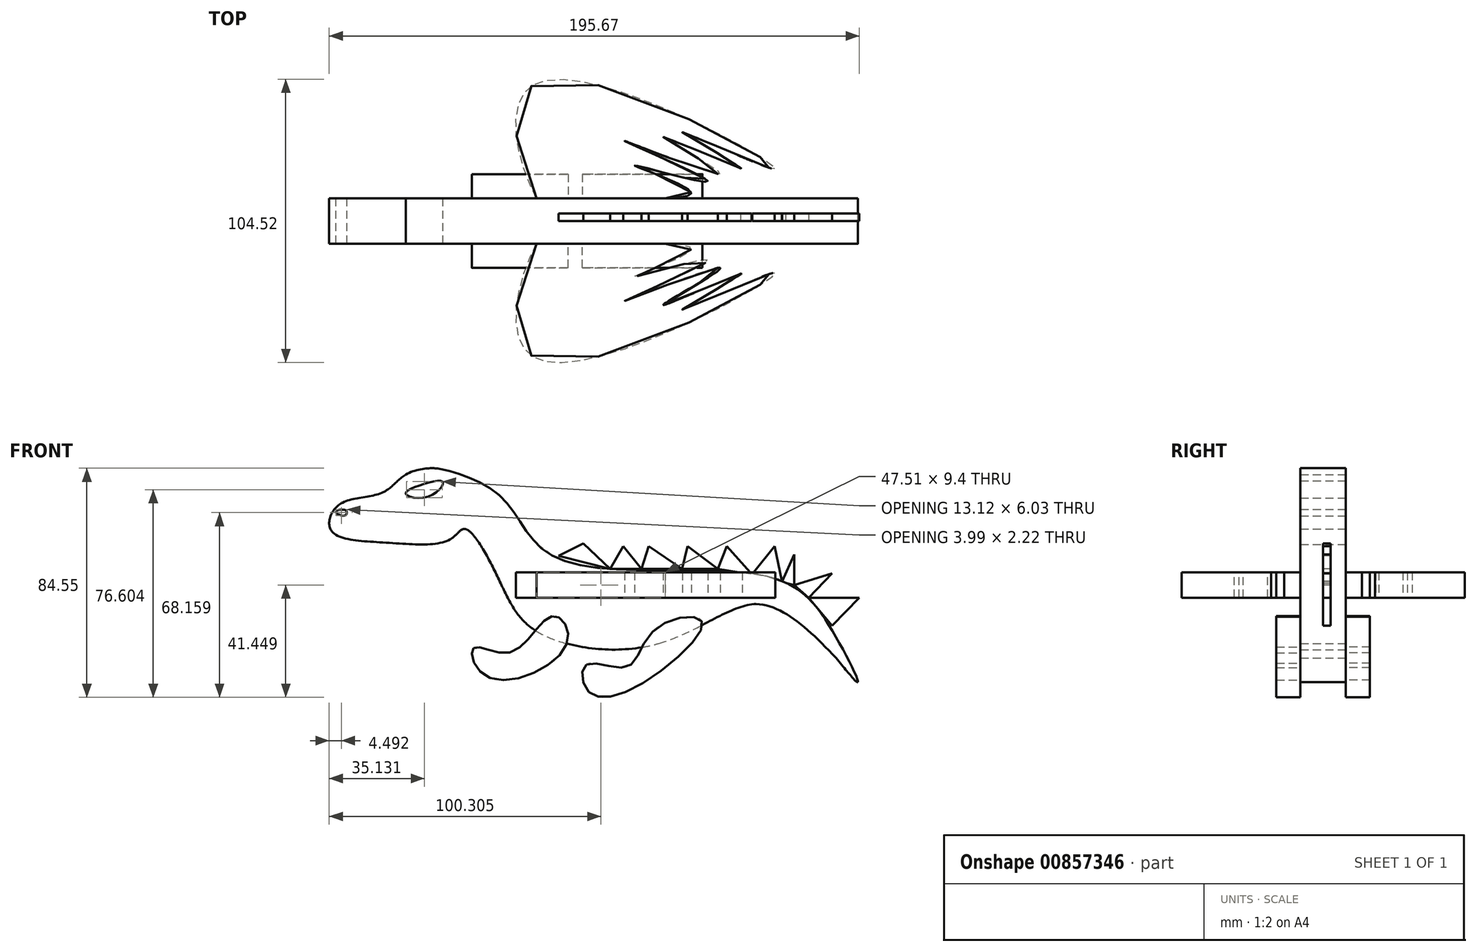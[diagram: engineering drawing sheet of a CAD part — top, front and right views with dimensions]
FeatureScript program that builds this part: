
annotation { "Feature Type Name" : "Feature", "Feature Type Description" : "" }
export const myFeature = defineFeature(function(context is Context, id is Id, definition is map)
    precondition{}
    {
        {
            var Q0;
            Q0=qCreatedBy(makeId("Front.planeOp"),FACE);
            var sketch = newSketch(context, id + "F0", { "sketchPlane" : qUnion([Q0])});
            skFitSpline(sketch, "E0", {"points": [v(-25.27, 47.3) * mm, v(-38.9, 45.42) * mm, v(-47.76, 38.67) * mm, v(-63.4, 34.35) * mm, v(-66.48, 24.9) * mm, v(-46.39, 20.32) * mm, v(-22.47, 21.54) * mm, v(-17.06, 25.35) * mm, v(-4.8, 7.29) * mm, v(9.15, -12.25) * mm, v(54.43, -16.9) * mm, v(90.4, -2.33) * mm, v(127.94, -31.19) * mm], "startDerivative": vector(-232.24, 20.13) * mm, "endDerivative": vector(316, -354.03) * mm});
            skFitSpline(sketch, "E1", {"points": [v(127.94, -31.19) * mm, v(118.93, -12.87) * mm, v(94.12, 7.9) * mm, v(16.6, 14.73) * mm, v(-3.57, 37.06) * mm, v(-25.27, 47.3) * mm, v(-30.43, 47.74) * mm, v(-38.9, 45.42) * mm, v(-47.76, 38.67) * mm, v(-63.4, 34.35) * mm, v(-66.48, 24.9) * mm, v(-46.39, 20.32) * mm, v(-22.47, 21.54) * mm, v(-17.06, 25.35) * mm, v(-4.8, 7.29) * mm, v(9.15, -12.25) * mm, v(54.43, -16.9) * mm, v(90.4, -2.33) * mm, v(114.92, -16.6) * mm, v(127.94, -31.19) * mm]});
            skFitSpline(sketch, "E2", {"points": [v(-33.96, 41.4) * mm, v(-25.27, 42.64) * mm, v(-30.43, 37.37) * mm, v(-38.9, 38.3) * mm, v(-33.96, 41.4) * mm]});
            skLineSegment(sketch, "E3", {"start": v(-67.1, 28.32) * mm, "end": v(-56.1, 26.68) * mm});
            skLineSegment(sketch, "E4", {"start": v(-56.1, 26.68) * mm, "end": v(-53.72, 26.68) * mm});
            skLineSegment(sketch, "E5", {"start": v(-53.72, 26.68) * mm, "end": v(-53.72, 24.9) * mm});
            skLineSegment(sketch, "E6", {"start": v(-53.72, 24.9) * mm, "end": v(-53.72, 23.27) * mm});
            skLineSegment(sketch, "E7", {"start": v(-53.72, 23.27) * mm, "end": v(-66.48, 24.9) * mm});
            skFitSpline(sketch, "E8", {"points": [v(-64.66, 31.7) * mm, v(-61.06, 32.17) * mm, v(-61.4, 30.3) * mm, v(-64.66, 31.7) * mm]});
            skSolve(sketch);
        }
        {
            var Q0;
            Q0 = qSketchRegion(id + "F0", true);
            extrude(context, id + "F1", {"entities" : qUnion([Q0]), "endBound" : BoundingType.SYMMETRIC, "depth" : 16.76 * mm, "offsetDistance" : 25.4 * mm});
        }
        {
            var Q0;
            Q0=qCreatedBy(makeId("Top.planeOp"),FACE);
            var sketch = newSketch(context, id + "F2", { "sketchPlane" : qUnion([Q0])});
            skFitSpline(sketch, "E9", {"points": [v(15.55, 0) * mm, v(9.19, -50.76) * mm, v(97.38, -19.17) * mm, v(63.16, -32.77) * mm, v(85.32, -19.39) * mm, v(56.14, -31.01) * mm, v(77.2, -17.41) * mm, v(41.88, -29.48) * mm, v(72.6, -14.56) * mm, v(45.6, -20.48) * mm, v(66.3, -10.77) * mm, v(43.9, -7.25) * mm, v(28.93, 0) * mm, v(15.55, 0) * mm]});
            skFitSpline(sketch, "E10.MirrorC", {"points": [v(15.55, 0) * mm, v(9.19, 50.76) * mm, v(97.38, 19.17) * mm, v(63.16, 32.77) * mm, v(85.32, 19.39) * mm, v(56.14, 31.01) * mm, v(77.2, 17.41) * mm, v(41.88, 29.48) * mm, v(72.6, 14.56) * mm, v(45.6, 20.48) * mm, v(66.3, 10.77) * mm, v(43.9, 7.25) * mm, v(28.93, 0) * mm, v(15.55, 0) * mm]});
            skSolve(sketch);
        }
        {
            var Q0;
            Q0 = qSketchRegion(id + "F2", true);
            extrude(context, id + "F3", {"entities" : qUnion([Q0]), "operationType" : NewBodyOperationType.ADD, "depth" : 9.4 * mm, "offsetDistance" : 25.4 * mm});
        }
        {
            var Q0;
            {var subQ0=sQuery(id+"F0.wireOp",EDGE,"E0");var subQ1=sQuery(id+"F0.wireOp",EDGE,"E1");var subQ8=sQuery(id+"F0.wireOp",EDGE,"E0");var subQ10=sQuery(id+"F2.wireOp",EDGE,"9c3de7f5-6968-4319-936d-da682d65bc910.MirrorC");Q0=makeQuery(id+"F3.boolean.opBoolean","SPLIT",FACE,{"disambiguationData":[TD([makeQuery(id+"F3.opExtrude","SWEPT_FACE",FACE,{"disambiguationData":[OSD([subQ10])]})])],"derivedFrom":makeQuery(id+"F1.opExtrude","CAP_FACE",FACE,{"disambiguationData":[OSD([subQ8,subQ1,sQuery(id+"F0.wireOp",EDGE,"E2"),sQuery(id+"F0.wireOp",EDGE,"E3"),sQuery(id+"F0.wireOp",EDGE,"E4"),sQuery(id+"F0.wireOp",EDGE,"E5"),sQuery(id+"F0.wireOp",EDGE,"E6"),sQuery(id+"F0.wireOp",EDGE,"E7"),sQuery(id+"F0.wireOp",EDGE,"E8"),subQ0])],"isStart":false})});}
            var sketch = newSketch(context, id + "F4", { "sketchPlane" : qUnion([Q0])});
            skSolve(sketch);
        }
        {
            var Q0;
            Q0 = qSketchRegion(id + "F2", true);
            extrude(context, id + "F5", {"entities" : qUnion([Q0]), "operationType" : NewBodyOperationType.ADD, "depth" : 6.6 * mm, "offsetDistance" : 25.4 * mm});
        }
        {
            var Q0;
            {var subQ11=sQuery(id+"F0.wireOp",EDGE,"E0");Q0=makeQuery(id+"F4.imprint","IMPRINT",FACE,{"disambiguationData":[TD([[makeQuery(id+"F4.imprint","IMPRINT",EDGE,{"derivedFrom":makeQuery(id+"F1.opExtrude","CAP_EDGE",EDGE,{"disambiguationData":[OSD([subQ11])],"isStart":false})}),1.0]])]});}
            var sketch = newSketch(context, id + "F6", { "sketchPlane" : qUnion([Q0])});
            skFitSpline(sketch, "E11", {"points": [v(-13.81, -18.59) * mm, v(-8.29, -29.46) * mm, v(20.64, -16.74) * mm, v(15.3, -6.8) * mm, v(0, -20.06) * mm, v(-13.81, -18.59) * mm]});
            skFitSpline(sketch, "E12", {"points": [v(27.82, -24.67) * mm, v(28.19, -34.25) * mm, v(46.43, -32.77) * mm, v(70.38, -8.82) * mm, v(53.24, -11.59) * mm, v(42.56, -25.59) * mm, v(27.82, -24.67) * mm]});
            skSolve(sketch);
        }
        {
            var Q0;
            Q0 = qSketchRegion(id + "F6", true);
            extrude(context, id + "F7", {"entities" : qUnion([Q0]), "operationType" : NewBodyOperationType.ADD, "depth" : 8.9 * mm, "offsetDistance" : 25.4 * mm});
        }
        {
            var Q0;
            Q0=makeQuery(id+"F1.opExtrude","SWEPT_BODY",BODY,{"disambiguationData":[OSD([sQuery(id+"F0.wireOp",EDGE,"E0"),sQuery(id+"F0.wireOp",EDGE,"E1"),sQuery(id+"F0.wireOp",EDGE,"E2"),sQuery(id+"F0.wireOp",EDGE,"E3"),sQuery(id+"F0.wireOp",EDGE,"E4"),sQuery(id+"F0.wireOp",EDGE,"E5"),sQuery(id+"F0.wireOp",EDGE,"E6"),sQuery(id+"F0.wireOp",EDGE,"E7"),sQuery(id+"F0.wireOp",EDGE,"E8"),sQuery(id+"F0.wireOp",EDGE,"E0")])]});
            var Q1;
            Q1=qCreatedBy(makeId("Front.planeOp"),FACE);
            mirror(context, id + "F8", {"operationType" : NewBodyOperationType.ADD, "entities" : qUnion([Q0]), "mirrorPlane" : qUnion([Q1])});
        }
        {
            var Q0;
            Q0=qCreatedBy(makeId("Front.planeOp"),FACE);
            var sketch = newSketch(context, id + "F9", { "sketchPlane" : qUnion([Q0])});
            skLineSegment(sketch, "E13", {"start": v(17.47, 15.47) * mm, "end": v(26.66, 19.96) * mm});
            skLineSegment(sketch, "E14", {"start": v(26.66, 19.96) * mm, "end": v(36.57, 10.63) * mm});
            skLineSegment(sketch, "E15", {"start": v(36.57, 10.63) * mm, "end": v(41.34, 18.95) * mm});
            skLineSegment(sketch, "E16", {"start": v(41.34, 18.95) * mm, "end": v(48.08, 10.63) * mm});
            skLineSegment(sketch, "E17", {"start": v(48.08, 10.63) * mm, "end": v(50.72, 18.95) * mm});
            skLineSegment(sketch, "E18", {"start": v(50.72, 18.95) * mm, "end": v(63.12, 10.63) * mm});
            skLineSegment(sketch, "E19", {"start": v(63.12, 10.63) * mm, "end": v(65.15, 18.95) * mm});
            skLineSegment(sketch, "E20", {"start": v(65.15, 18.95) * mm, "end": v(76.31, 10.63) * mm});
            skLineSegment(sketch, "E21", {"start": v(76.31, 10.63) * mm, "end": v(79.63, 18.95) * mm});
            skLineSegment(sketch, "E22", {"start": v(79.63, 18.95) * mm, "end": v(88.9, 8.67) * mm});
            skLineSegment(sketch, "E23", {"start": v(88.9, 8.67) * mm, "end": v(97.23, 18.95) * mm});
            skLineSegment(sketch, "E24", {"start": v(97.23, 18.95) * mm, "end": v(99.99, 5.84) * mm});
            skLineSegment(sketch, "E25", {"start": v(99.99, 5.84) * mm, "end": v(104.53, 15.89) * mm});
            skLineSegment(sketch, "E26", {"start": v(104.53, 15.89) * mm, "end": v(104.53, 4.62) * mm});
            skLineSegment(sketch, "E27", {"start": v(104.53, 4.62) * mm, "end": v(118.5, 9) * mm});
            skLineSegment(sketch, "E28", {"start": v(118.5, 9) * mm, "end": v(109.8, 0) * mm});
            skLineSegment(sketch, "E29", {"start": v(109.8, 0) * mm, "end": v(128.5, 0) * mm});
            skLineSegment(sketch, "E30", {"start": v(128.5, 0) * mm, "end": v(118.5, -10.36) * mm});
            skLineSegment(sketch, "E31", {"start": v(17.47, 15.47) * mm, "end": v(36.57, 10.63) * mm});
            skLineSegment(sketch, "E32", {"start": v(36.57, 10.63) * mm, "end": v(48.08, 10.63) * mm});
            skLineSegment(sketch, "E33", {"start": v(63.12, 10.63) * mm, "end": v(76.31, 10.63) * mm});
            skLineSegment(sketch, "E34", {"start": v(48.08, 10.63) * mm, "end": v(63.12, 10.63) * mm});
            skLineSegment(sketch, "E35", {"start": v(76.31, 10.63) * mm, "end": v(88.9, 8.67) * mm});
            skLineSegment(sketch, "E36", {"start": v(88.9, 8.67) * mm, "end": v(99.99, 5.84) * mm});
            skLineSegment(sketch, "E37", {"start": v(99.99, 5.84) * mm, "end": v(104.53, 4.62) * mm});
            skLineSegment(sketch, "E38", {"start": v(104.53, 4.62) * mm, "end": v(109.8, 0) * mm});
            skLineSegment(sketch, "E39", {"start": v(109.8, 0) * mm, "end": v(118.5, -10.36) * mm});
            skSolve(sketch);
        }
        {
            var Q0;
            Q0 = qSketchRegion(id + "F9", true);
            extrude(context, id + "F10", {"entities" : qUnion([Q0]), "operationType" : NewBodyOperationType.ADD, "flatOperationType" : FlatOperationType.REMOVE, "oppositeDirection" : true, "depth" : 2.8 * mm, "offsetDistance" : 25.4 * mm, "domain" : OperationDomain.MODEL});
        }
    });
